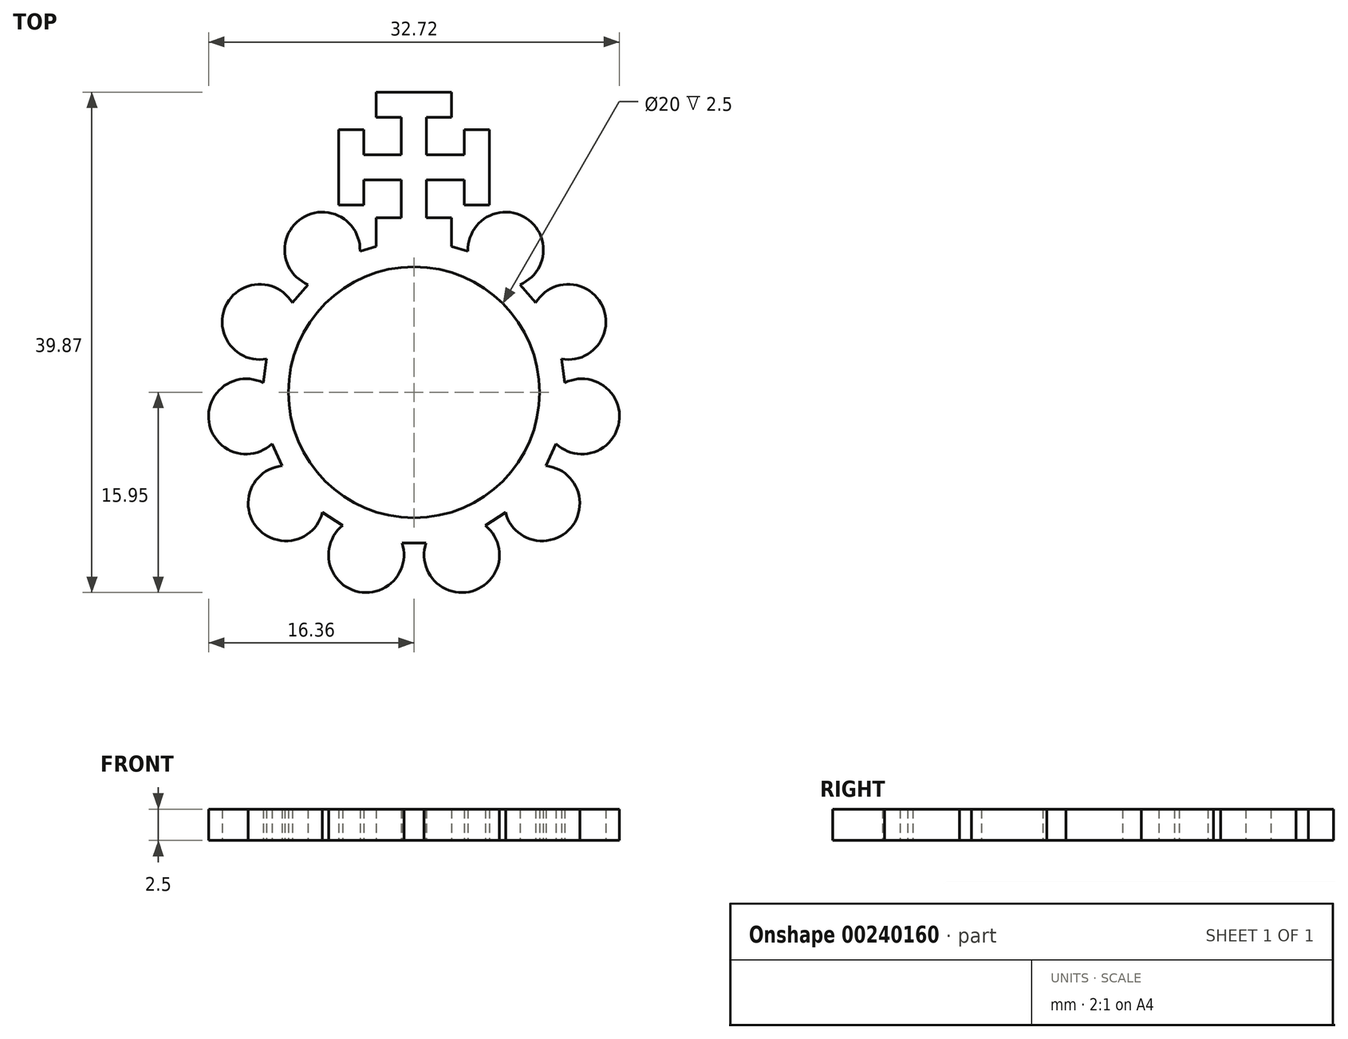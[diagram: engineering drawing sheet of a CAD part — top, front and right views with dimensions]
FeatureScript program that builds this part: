
annotation { "Feature Type Name" : "Feature", "Feature Type Description" : "" }
export const myFeature = defineFeature(function(context is Context, id is Id, definition is map)
    precondition{}
    {
        {
            var Q0;
            Q0=qCreatedBy(makeId("Top.planeOp"),FACE);
            var sketch = newSketch(context, id + "F0", { "sketchPlane" : qUnion([Q0])});
            skCircle(sketch, "E0", {"center": v(0, 0) * mm, "radius": 10 * mm});
            skLineSegment(sketch, "E1.0", {"start": v(3, 11.62) * mm, "end": v(4.3, 11.24) * mm});
            skLineSegment(sketch, "E1.1", {"start": v(8.43, 8.58) * mm, "end": v(9.7, 7.13) * mm});
            skLineSegment(sketch, "E1.2", {"start": v(11.73, 2.66) * mm, "end": v(12, 0.76) * mm});
            skLineSegment(sketch, "E1.3", {"start": v(11.3, -4.1) * mm, "end": v(10.51, -5.86) * mm});
            skLineSegment(sketch, "E1.4", {"start": v(7.3, -9.57) * mm, "end": v(5.68, -10.6) * mm});
            skLineSegment(sketch, "E1.5", {"start": v(0.96, -12) * mm, "end": v(-0.96, -12) * mm});
            skLineSegment(sketch, "E1.6", {"start": v(-5.68, -10.6) * mm, "end": v(-7.3, -9.57) * mm});
            skLineSegment(sketch, "E1.7", {"start": v(-10.51, -5.86) * mm, "end": v(-11.3, -4.1) * mm});
            skLineSegment(sketch, "E1.8", {"start": v(-12, 0.76) * mm, "end": v(-11.73, 2.66) * mm});
            skLineSegment(sketch, "E1.9", {"start": v(-9.7, 7.13) * mm, "end": v(-8.43, 8.58) * mm});
            skLineSegment(sketch, "E1.10", {"start": v(-4.3, 11.24) * mm, "end": v(-3, 11.62) * mm});
            skArc(sketch, "E2", {"start": v(8.43, 8.58) * mm, "mid": v(8.92, 13.88) * mm, "end": v(4.3, 11.24) * mm});
            skArc(sketch, "E3.2.0", {"start": v(-4.3, 11.24) * mm, "mid": v(-8.92, 13.88) * mm, "end": v(-8.43, 8.58) * mm});
            skArc(sketch, "E3.3.0", {"start": v(-9.7, 7.13) * mm, "mid": v(-15, 6.85) * mm, "end": v(-11.73, 2.66) * mm});
            skArc(sketch, "E3.4.0", {"start": v(-12, 0.76) * mm, "mid": v(-16.33, -2.35) * mm, "end": v(-11.3, -4.1) * mm});
            skArc(sketch, "E3.5.0", {"start": v(-10.51, -5.86) * mm, "mid": v(-12.47, -10.8) * mm, "end": v(-7.3, -9.57) * mm});
            skArc(sketch, "E3.6.0", {"start": v(-5.68, -10.6) * mm, "mid": v(-4.65, -15.83) * mm, "end": v(-0.96, -12) * mm});
            skArc(sketch, "E3.7.0", {"start": v(0.96, -12) * mm, "mid": v(4.65, -15.83) * mm, "end": v(5.68, -10.6) * mm});
            skArc(sketch, "E3.8.0", {"start": v(7.3, -9.57) * mm, "mid": v(12.47, -10.8) * mm, "end": v(10.51, -5.86) * mm});
            skArc(sketch, "E3.9.0", {"start": v(11.3, -4.1) * mm, "mid": v(16.33, -2.35) * mm, "end": v(12, 0.76) * mm});
            skArc(sketch, "E3.10.0", {"start": v(11.73, 2.66) * mm, "mid": v(15, 6.85) * mm, "end": v(9.7, 7.13) * mm});
            skLineSegment(sketch, "E4", {"start": v(3, 11.62) * mm, "end": v(3, 13.92) * mm});
            skLineSegment(sketch, "E5", {"start": v(3, 13.92) * mm, "end": v(1, 13.92) * mm});
            skLineSegment(sketch, "E6", {"start": v(1, 13.92) * mm, "end": v(1, 16.92) * mm});
            skLineSegment(sketch, "E7", {"start": v(1, 16.92) * mm, "end": v(4, 16.92) * mm});
            skLineSegment(sketch, "E8", {"start": v(4, 16.92) * mm, "end": v(4, 14.92) * mm});
            skLineSegment(sketch, "E9", {"start": v(4, 14.92) * mm, "end": v(6, 14.92) * mm});
            skLineSegment(sketch, "E10", {"start": v(6, 14.92) * mm, "end": v(6, 20.92) * mm});
            skLineSegment(sketch, "E11", {"start": v(6, 20.92) * mm, "end": v(4, 20.92) * mm});
            skLineSegment(sketch, "E12", {"start": v(4, 20.92) * mm, "end": v(4, 18.92) * mm});
            skLineSegment(sketch, "E13", {"start": v(4, 18.92) * mm, "end": v(1, 18.92) * mm});
            skLineSegment(sketch, "E14", {"start": v(1, 18.92) * mm, "end": v(1, 21.92) * mm});
            skLineSegment(sketch, "E15", {"start": v(1, 21.92) * mm, "end": v(3, 21.92) * mm});
            skLineSegment(sketch, "E16", {"start": v(3, 21.92) * mm, "end": v(3, 23.92) * mm});
            skLineSegment(sketch, "E17", {"start": v(3, 23.92) * mm, "end": v(0, 23.92) * mm});
            skLineSegment(sketch, "E18.MirrorCS", {"start": v(-3, 23.92) * mm, "end": v(0, 23.92) * mm});
            skLineSegment(sketch, "E19.MirrorCS", {"start": v(-3, 21.92) * mm, "end": v(-3, 23.92) * mm});
            skLineSegment(sketch, "E20.MirrorCS", {"start": v(-1, 21.92) * mm, "end": v(-3, 21.92) * mm});
            skLineSegment(sketch, "E21.MirrorCS", {"start": v(-1, 18.92) * mm, "end": v(-1, 21.92) * mm});
            skLineSegment(sketch, "E22.MirrorCS", {"start": v(-4, 18.92) * mm, "end": v(-1, 18.92) * mm});
            skLineSegment(sketch, "E23.MirrorCS", {"start": v(-4, 20.92) * mm, "end": v(-4, 18.92) * mm});
            skLineSegment(sketch, "E24.MirrorCS", {"start": v(-6, 20.92) * mm, "end": v(-4, 20.92) * mm});
            skLineSegment(sketch, "E25.MirrorCS", {"start": v(-6, 14.92) * mm, "end": v(-6, 20.92) * mm});
            skLineSegment(sketch, "E26.MirrorCS", {"start": v(-1, 16.92) * mm, "end": v(-4, 16.92) * mm});
            skLineSegment(sketch, "E27.MirrorCS", {"start": v(-4, 16.92) * mm, "end": v(-4, 14.92) * mm});
            skLineSegment(sketch, "E28.MirrorCS", {"start": v(-1, 13.92) * mm, "end": v(-1, 16.92) * mm});
            skLineSegment(sketch, "E29.MirrorCS", {"start": v(-4, 14.92) * mm, "end": v(-6, 14.92) * mm});
            skLineSegment(sketch, "E30.MirrorCS", {"start": v(-3, 13.92) * mm, "end": v(-1, 13.92) * mm});
            skLineSegment(sketch, "E31.MirrorCS", {"start": v(-3, 11.62) * mm, "end": v(-3, 13.92) * mm});
            skPoint(sketch, "E32.orphan", {"position": v(-3, 11.92) * mm});
            skPoint(sketch, "E33.MirrorCS.start.orphan", {"position": v(0, 12.5) * mm});
            skPoint(sketch, "E34.end.orphan", {"position": v(3, 11.92) * mm});
            skSolve(sketch);
        }
        {
            var Q0;
            Q0 = qSketchRegion(id + "F0", true);
            extrude(context, id + "F1", {"entities" : qUnion([Q0]), "depth" : 2.5 * mm});
        }
    });
